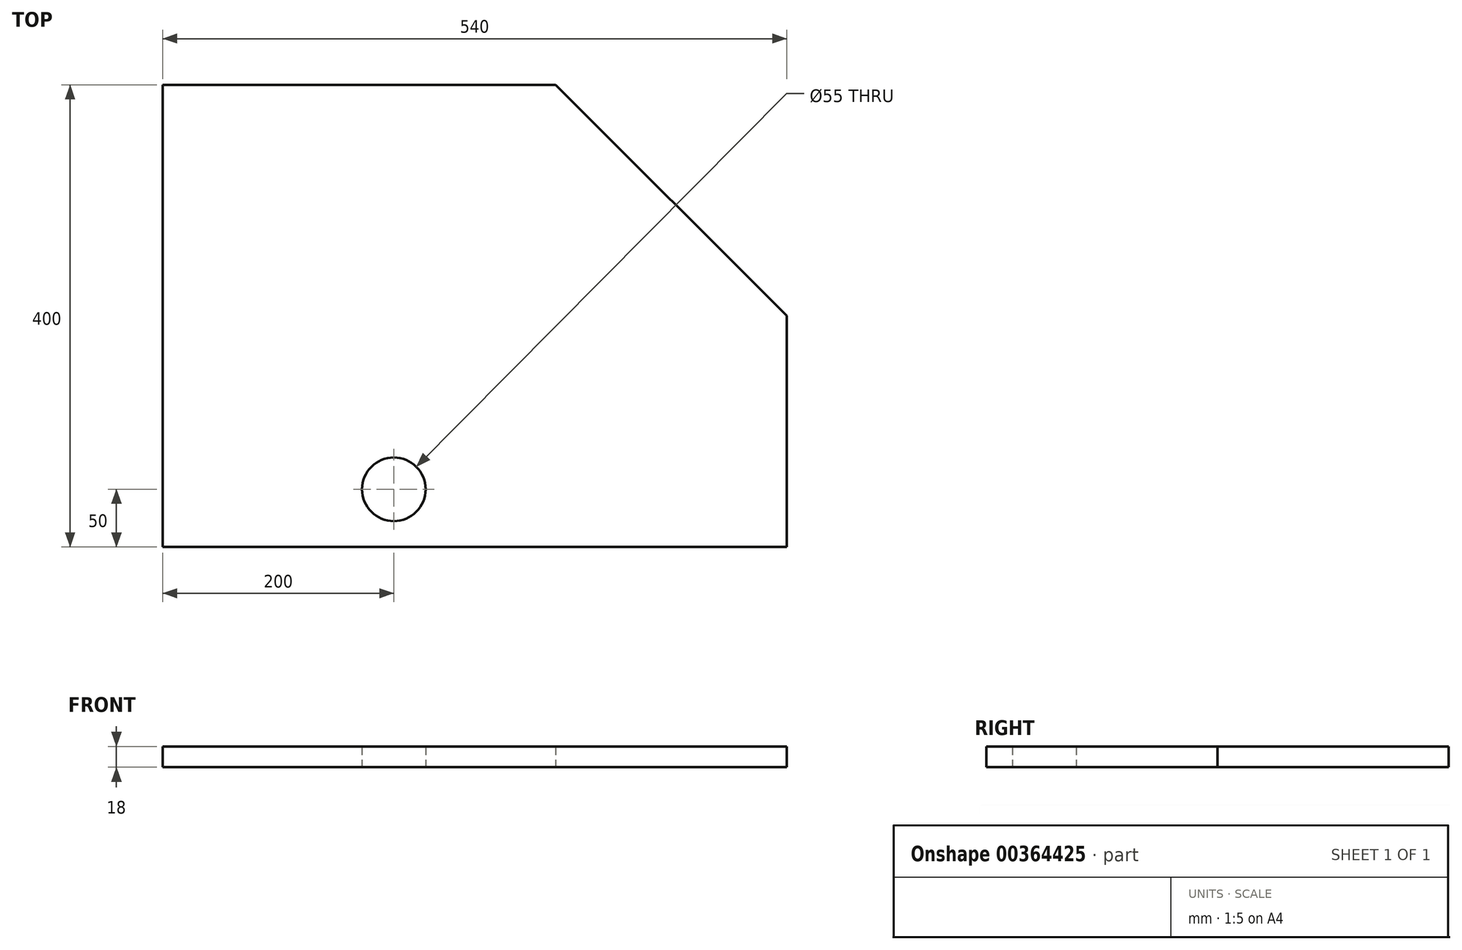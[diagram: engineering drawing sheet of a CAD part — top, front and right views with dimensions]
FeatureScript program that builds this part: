
annotation { "Feature Type Name" : "Feature", "Feature Type Description" : "" }
export const myFeature = defineFeature(function(context is Context, id is Id, definition is map)
    precondition{}
    {
        {
            var Q0;
            Q0=qCreatedBy(makeId("Top.planeOp"),FACE);
            var sketch = newSketch(context, id + "F0", { "sketchPlane" : qUnion([Q0])});
            skLineSegment(sketch, "E0.bottom", {"start": v(0, 0) * mm, "end": v(540, 0) * mm});
            skLineSegment(sketch, "E0.left", {"start": v(0, 0) * mm, "end": v(0, 400) * mm});
            skLineSegment(sketch, "E0.right", {"start": v(540, 0) * mm, "end": v(540, 200) * mm});
            skLineSegment(sketch, "E1", {"start": v(0, 400) * mm, "end": v(340, 400) * mm});
            skLineSegment(sketch, "E2", {"start": v(340, 400) * mm, "end": v(540, 200) * mm});
            skCircle(sketch, "E3", {"center": v(200, 50) * mm, "radius": 27.5 * mm});
            skSolve(sketch);
        }
        {
            var Q0;
            Q0=makeQuery(id+"F0.imprint","IMPRINT",FACE,{"disambiguationData":[TD([[makeQuery(id+"F0.imprint","IMPRINT",EDGE,{"derivedFrom":sQuery(id+"F0.wireOp",EDGE,"E0.bottom")}),1.0]])]});
            extrude(context, id + "F1", {"entities" : qUnion([Q0]), "depth" : 18 * mm});
        }
    });
